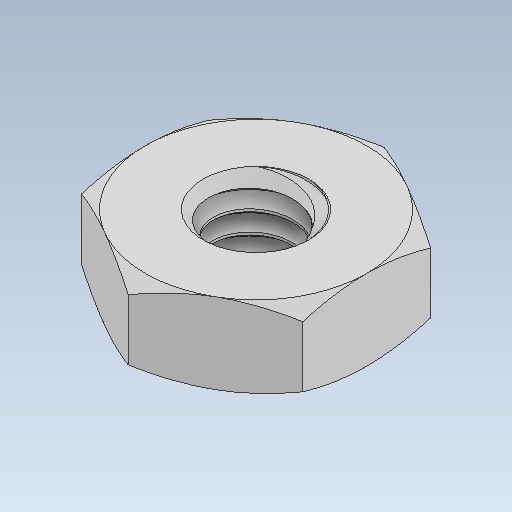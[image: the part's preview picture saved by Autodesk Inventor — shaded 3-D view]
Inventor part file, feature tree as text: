
AUTODESK INVENTOR PART (.ipt)
format: ipt  version: 2021 (Build 250183000, 183)  size: 268,800 bytes
history: native  units: mm
features: mirror x1
ambient origin geometry x8: Origin, YZ Plane, XZ Plane, XY Plane, X Axis, Y Axis, Z Axis, Center Point
bodies: Solid1 (feature_tree)
feature tree (1):
  mirror  "Mirror1"
